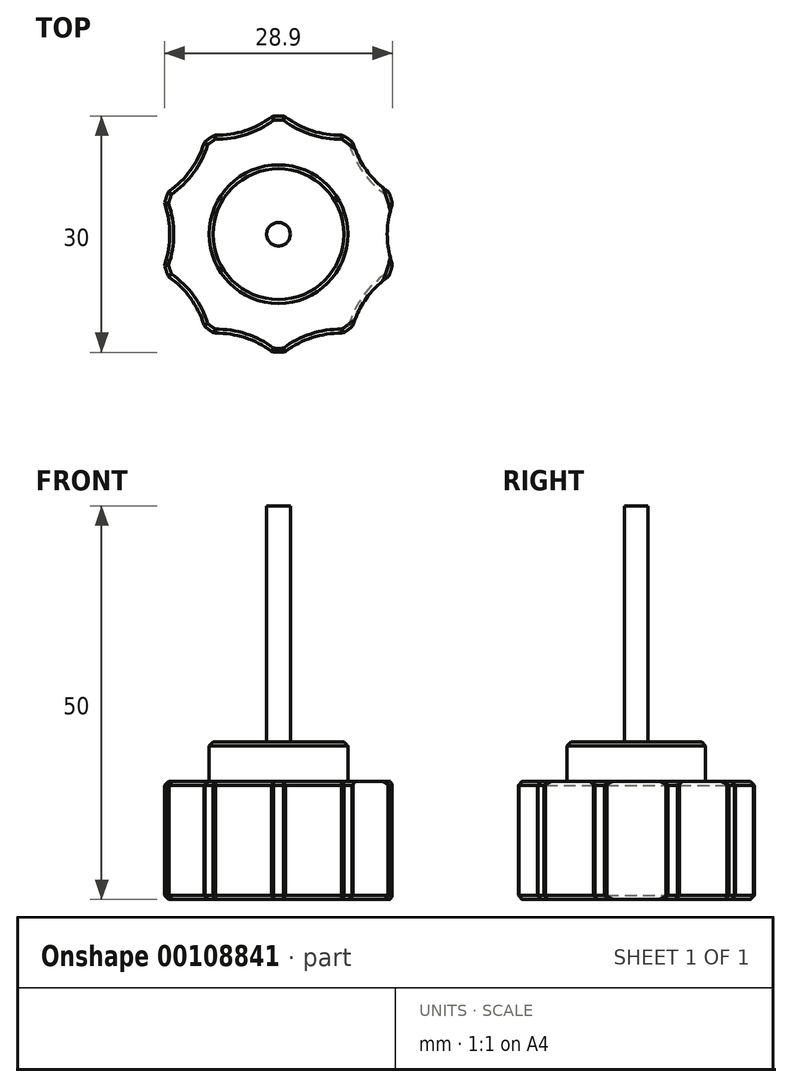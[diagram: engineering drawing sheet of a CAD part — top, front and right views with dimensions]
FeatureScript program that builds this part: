
annotation { "Feature Type Name" : "Feature", "Feature Type Description" : "" }
export const myFeature = defineFeature(function(context is Context, id is Id, definition is map)
    precondition{}
    {
        {
            var Q0;
            Q0=qCreatedBy(makeId("Top.planeOp"),FACE);
            var sketch = newSketch(context, id + "F0", { "sketchPlane" : qUnion([Q0])});
            skLineSegment(sketch, "E0", {"start": v(0, 24.73) * mm, "end": v(0, -28.06) * mm, "construction": true});
            skLineSegment(sketch, "E1", {"start": v(-17.48, 0) * mm, "end": v(21.6, 0) * mm, "construction": true});
            skArc(sketch, "E2", {"start": v(-14, 5.38) * mm, "mid": v(-14.27, 4.64) * mm, "end": v(-14.49, 3.88) * mm});
            skLineSegment(sketch, "E3", {"start": v(0, 0) * mm, "end": v(21.8, 5.84) * mm, "construction": true});
            skLineSegment(sketch, "E4.MirrorCS", {"start": v(0, 0) * mm, "end": v(21.8, -5.84) * mm, "construction": true});
            skArc(sketch, "E5", {"start": v(14.49, 3.88) * mm, "mid": v(13.81, 0) * mm, "end": v(14.49, -3.88) * mm});
            skLineSegment(sketch, "E6.anchor1", {"start": v(0, 0) * mm, "end": v(14.49, -3.88) * mm, "construction": true});
            skLineSegment(sketch, "E6.anchor2", {"start": v(0, 0) * mm, "end": v(14.49, -3.88) * mm, "construction": true});
            skArc(sketch, "E7.1.0", {"start": v(9.44, 11.66) * mm, "mid": v(11.17, 8.12) * mm, "end": v(14, 5.38) * mm});
            skArc(sketch, "E7.2.0", {"start": v(0.79, 14.98) * mm, "mid": v(4.27, 13.14) * mm, "end": v(8.17, 12.58) * mm});
            skArc(sketch, "E7.3.0", {"start": v(-8.17, 12.58) * mm, "mid": v(-4.27, 13.14) * mm, "end": v(-0.79, 14.98) * mm});
            skArc(sketch, "E7.4.0", {"start": v(-14, 5.38) * mm, "mid": v(-11.17, 8.12) * mm, "end": v(-9.44, 11.66) * mm});
            skArc(sketch, "E7.5.0", {"start": v(-14.49, -3.88) * mm, "mid": v(-13.81, 0) * mm, "end": v(-14.49, 3.88) * mm});
            skArc(sketch, "E7.6.0", {"start": v(-9.44, -11.66) * mm, "mid": v(-11.17, -8.12) * mm, "end": v(-14, -5.38) * mm});
            skArc(sketch, "E7.7.0", {"start": v(-0.79, -14.98) * mm, "mid": v(-4.27, -13.14) * mm, "end": v(-8.17, -12.58) * mm});
            skArc(sketch, "E7.8.0", {"start": v(8.17, -12.58) * mm, "mid": v(4.27, -13.14) * mm, "end": v(0.79, -14.98) * mm});
            skArc(sketch, "E7.9.0", {"start": v(14, -5.38) * mm, "mid": v(11.17, -8.12) * mm, "end": v(9.44, -11.66) * mm});
            skArc(sketch, "E8.trimOffspring", {"start": v(-8.17, 12.58) * mm, "mid": v(-8.82, 12.14) * mm, "end": v(-9.44, 11.66) * mm});
            skArc(sketch, "E9.trimOffspring", {"start": v(0.79, 14.98) * mm, "mid": v(0, 15) * mm, "end": v(-0.79, 14.98) * mm});
            skArc(sketch, "E10.trimOffspring", {"start": v(9.44, 11.66) * mm, "mid": v(8.82, 12.14) * mm, "end": v(8.17, 12.58) * mm});
            skArc(sketch, "E11.trimOffspring", {"start": v(14.49, 3.88) * mm, "mid": v(14.27, 4.64) * mm, "end": v(14, 5.38) * mm});
            skArc(sketch, "E12.trimOffspring", {"start": v(14, -5.38) * mm, "mid": v(14.27, -4.64) * mm, "end": v(14.49, -3.88) * mm});
            skArc(sketch, "E13.trimOffspring", {"start": v(8.17, -12.58) * mm, "mid": v(8.82, -12.14) * mm, "end": v(9.44, -11.66) * mm});
            skArc(sketch, "E14.trimOffspring", {"start": v(-0.79, -14.98) * mm, "mid": v(0, -15) * mm, "end": v(0.79, -14.98) * mm});
            skArc(sketch, "E15.trimOffspring", {"start": v(-9.44, -11.66) * mm, "mid": v(-8.82, -12.14) * mm, "end": v(-8.17, -12.58) * mm});
            skArc(sketch, "E16.trimOffspring", {"start": v(-14.49, -3.88) * mm, "mid": v(-14.27, -4.64) * mm, "end": v(-14, -5.38) * mm});
            skSolve(sketch);
        }
        {
            var Q0;
            Q0=makeQuery(id+"F0.imprint","IMPRINT",FACE,{"disambiguationData":[TD([[makeQuery(id+"F0.imprint","IMPRINT",EDGE,{"derivedFrom":sQuery(id+"F0.wireOp",EDGE,"E2")}),1.0]])]});
            extrude(context, id + "F1", {"entities" : qUnion([Q0]), "depth" : 15 * mm});
        }
        {
            var Q0;
            Q0=makeQuery(id+"F1.opExtrude","CAP_FACE",FACE,{"disambiguationData":[OSD([sQuery(id+"F0.wireOp",EDGE,"E2"),sQuery(id+"F0.wireOp",EDGE,"E5"),sQuery(id+"F0.wireOp",EDGE,"E7.1.0"),sQuery(id+"F0.wireOp",EDGE,"E7.2.0"),sQuery(id+"F0.wireOp",EDGE,"E7.3.0"),sQuery(id+"F0.wireOp",EDGE,"E7.4.0"),sQuery(id+"F0.wireOp",EDGE,"E7.5.0"),sQuery(id+"F0.wireOp",EDGE,"E7.6.0"),sQuery(id+"F0.wireOp",EDGE,"E7.7.0"),sQuery(id+"F0.wireOp",EDGE,"E7.8.0"),sQuery(id+"F0.wireOp",EDGE,"E7.9.0"),sQuery(id+"F0.wireOp",EDGE,"E8.trimOffspring"),sQuery(id+"F0.wireOp",EDGE,"E9.trimOffspring"),sQuery(id+"F0.wireOp",EDGE,"E10.trimOffspring"),sQuery(id+"F0.wireOp",EDGE,"E11.trimOffspring"),sQuery(id+"F0.wireOp",EDGE,"E12.trimOffspring"),sQuery(id+"F0.wireOp",EDGE,"E13.trimOffspring"),sQuery(id+"F0.wireOp",EDGE,"E14.trimOffspring"),sQuery(id+"F0.wireOp",EDGE,"E15.trimOffspring"),sQuery(id+"F0.wireOp",EDGE,"E16.trimOffspring")])],"isStart":false});
            cPlane(context, id + "F2", {"entities" : qUnion([Q0]), "cplaneType" : CPlaneType.OFFSET, "offset" : 0 * mm, "width" : 150 * mm, "height" : 150 * mm});
        }
        {
            var Q0;
            Q0=qCreatedBy(id+"F2.planeOp",FACE);
            var sketch = newSketch(context, id + "F3", { "sketchPlane" : qUnion([Q0])});
            skCircle(sketch, "E17", {"center": v(0, 0) * mm, "radius": 8.8 * mm});
            skSolve(sketch);
        }
        {
            var Q0;
            Q0 = qSketchRegion(id + "F3", true);
            extrude(context, id + "F4", {"entities" : qUnion([Q0]), "operationType" : NewBodyOperationType.ADD, "depth" : 5 * mm});
        }
        {
            var Q0;
            Q0=makeQuery(id+"F4.opExtrude","CAP_FACE",FACE,{"disambiguationData":[OSD([sQuery(id+"F3.wireOp",EDGE,"E17")])],"isStart":false});
            cPlane(context, id + "F5", {"entities" : qUnion([Q0]), "cplaneType" : CPlaneType.OFFSET, "offset" : 0 * mm, "width" : 150 * mm, "height" : 150 * mm});
        }
        {
            var Q0;
            Q0=qCreatedBy(id+"F5.planeOp",FACE);
            var sketch = newSketch(context, id + "F6", { "sketchPlane" : qUnion([Q0])});
            skCircle(sketch, "E18", {"center": v(0, 0) * mm, "radius": 1.5 * mm});
            skSolve(sketch);
        }
        {
            var Q0;
            Q0=makeQuery(id+"F6.imprint","IMPRINT",FACE,{"disambiguationData":[TD([[makeQuery(id+"F6.imprint","IMPRINT",EDGE,{"derivedFrom":sQuery(id+"F6.wireOp",EDGE,"E18")}),1.0]])]});
            extrude(context, id + "F7", {"entities" : qUnion([Q0]), "depth" : 30 * mm});
        }
        {
            var Q0;
            Q0=makeQuery(id+"F4.opExtrude","CAP_EDGE",EDGE,{"disambiguationData":[OSD([sQuery(id+"F3.wireOp",EDGE,"E17")])],"isStart":false});
            var Q1;
            Q1=makeQuery(id+"F1.opExtrude","CAP_EDGE",EDGE,{"disambiguationData":[OSD([sQuery(id+"F0.wireOp",EDGE,"E7.4.0")])],"isStart":false});
            var Q2;
            Q2=makeQuery(id+"F1.opExtrude","CAP_EDGE",EDGE,{"disambiguationData":[OSD([sQuery(id+"F0.wireOp",EDGE,"E7.5.0")])],"isStart":false});
            var Q3;
            Q3=makeQuery(id+"F1.opExtrude","CAP_EDGE",EDGE,{"disambiguationData":[OSD([sQuery(id+"F0.wireOp",EDGE,"E16.trimOffspring")])],"isStart":false});
            var Q4;
            Q4=makeQuery(id+"F1.opExtrude","CAP_EDGE",EDGE,{"disambiguationData":[OSD([sQuery(id+"F0.wireOp",EDGE,"E2")])],"isStart":false});
            var Q5;
            Q5=makeQuery(id+"F1.opExtrude","CAP_EDGE",EDGE,{"disambiguationData":[OSD([sQuery(id+"F0.wireOp",EDGE,"E13.trimOffspring")])],"isStart":true});
            var Q6;
            Q6=makeQuery(id+"F1.opExtrude","CAP_EDGE",EDGE,{"disambiguationData":[OSD([sQuery(id+"F0.wireOp",EDGE,"E7.6.0")])],"isStart":false});
            var Q7;
            Q7=makeQuery(id+"F1.opExtrude","CAP_EDGE",EDGE,{"disambiguationData":[OSD([sQuery(id+"F0.wireOp",EDGE,"E15.trimOffspring")])],"isStart":false});
            var Q8;
            Q8=makeQuery(id+"F1.opExtrude","CAP_EDGE",EDGE,{"disambiguationData":[OSD([sQuery(id+"F0.wireOp",EDGE,"E13.trimOffspring")])],"isStart":false});
            var Q9;
            Q9=makeQuery(id+"F1.opExtrude","CAP_EDGE",EDGE,{"disambiguationData":[OSD([sQuery(id+"F0.wireOp",EDGE,"E7.7.0")])],"isStart":false});
            var Q10;
            Q10=makeQuery(id+"F1.opExtrude","CAP_EDGE",EDGE,{"disambiguationData":[OSD([sQuery(id+"F0.wireOp",EDGE,"E14.trimOffspring")])],"isStart":false});
            var Q11;
            Q11=makeQuery(id+"F1.opExtrude","CAP_EDGE",EDGE,{"disambiguationData":[OSD([sQuery(id+"F0.wireOp",EDGE,"E7.8.0")])],"isStart":false});
            var Q12;
            Q12=makeQuery(id+"F1.opExtrude","SWEPT_EDGE",EDGE,{"disambiguationData":[OSD([sQuery(id+"F0.wireOp",EDGE,"E7.8.0"),sQuery(id+"F0.wireOp",EDGE,"E13.trimOffspring")])]});
            var Q13;
            Q13=makeQuery(id+"F1.opExtrude","SWEPT_EDGE",EDGE,{"disambiguationData":[OSD([sQuery(id+"F0.wireOp",EDGE,"E7.9.0"),sQuery(id+"F0.wireOp",EDGE,"E13.trimOffspring")])]});
            var Q14;
            Q14=makeQuery(id+"F1.opExtrude","CAP_EDGE",EDGE,{"disambiguationData":[OSD([sQuery(id+"F0.wireOp",EDGE,"E11.trimOffspring")])],"isStart":false});
            var Q15;
            Q15=makeQuery(id+"F1.opExtrude","CAP_EDGE",EDGE,{"disambiguationData":[OSD([sQuery(id+"F0.wireOp",EDGE,"E5")])],"isStart":true});
            var Q16;
            Q16=makeQuery(id+"F1.opExtrude","CAP_EDGE",EDGE,{"disambiguationData":[OSD([sQuery(id+"F0.wireOp",EDGE,"E12.trimOffspring")])],"isStart":true});
            var Q17;
            Q17=makeQuery(id+"F1.opExtrude","CAP_EDGE",EDGE,{"disambiguationData":[OSD([sQuery(id+"F0.wireOp",EDGE,"E12.trimOffspring")])],"isStart":false});
            var Q18;
            Q18=makeQuery(id+"F1.opExtrude","CAP_EDGE",EDGE,{"disambiguationData":[OSD([sQuery(id+"F0.wireOp",EDGE,"E5")])],"isStart":false});
            var Q19;
            Q19=makeQuery(id+"F1.opExtrude","CAP_EDGE",EDGE,{"disambiguationData":[OSD([sQuery(id+"F0.wireOp",EDGE,"E7.1.0")])],"isStart":true});
            var Q20;
            Q20=makeQuery(id+"F1.opExtrude","SWEPT_EDGE",EDGE,{"disambiguationData":[OSD([sQuery(id+"F0.wireOp",EDGE,"E7.9.0"),sQuery(id+"F0.wireOp",EDGE,"E12.trimOffspring")])]});
            var Q21;
            Q21=makeQuery(id+"F1.opExtrude","SWEPT_EDGE",EDGE,{"disambiguationData":[OSD([sQuery(id+"F0.wireOp",EDGE,"E5"),sQuery(id+"F0.wireOp",EDGE,"E12.trimOffspring")])]});
            var Q22;
            Q22=makeQuery(id+"F1.opExtrude","SWEPT_EDGE",EDGE,{"disambiguationData":[OSD([sQuery(id+"F0.wireOp",EDGE,"E5"),sQuery(id+"F0.wireOp",EDGE,"E11.trimOffspring")])]});
            var Q23;
            Q23=makeQuery(id+"F1.opExtrude","SWEPT_EDGE",EDGE,{"disambiguationData":[OSD([sQuery(id+"F0.wireOp",EDGE,"E7.1.0"),sQuery(id+"F0.wireOp",EDGE,"E11.trimOffspring")])]});
            var Q24;
            Q24=makeQuery(id+"F1.opExtrude","CAP_EDGE",EDGE,{"disambiguationData":[OSD([sQuery(id+"F0.wireOp",EDGE,"E11.trimOffspring")])],"isStart":true});
            var Q25;
            Q25=makeQuery(id+"F1.opExtrude","CAP_EDGE",EDGE,{"disambiguationData":[OSD([sQuery(id+"F0.wireOp",EDGE,"E7.9.0")])],"isStart":true});
            var Q26;
            Q26=makeQuery(id+"F1.opExtrude","CAP_EDGE",EDGE,{"disambiguationData":[OSD([sQuery(id+"F0.wireOp",EDGE,"E10.trimOffspring")])],"isStart":false});
            var Q27;
            Q27=makeQuery(id+"F1.opExtrude","CAP_EDGE",EDGE,{"disambiguationData":[OSD([sQuery(id+"F0.wireOp",EDGE,"E9.trimOffspring")])],"isStart":false});
            var Q28;
            Q28=makeQuery(id+"F1.opExtrude","CAP_EDGE",EDGE,{"disambiguationData":[OSD([sQuery(id+"F0.wireOp",EDGE,"E7.3.0")])],"isStart":false});
            var Q29;
            Q29=makeQuery(id+"F1.opExtrude","CAP_EDGE",EDGE,{"disambiguationData":[OSD([sQuery(id+"F0.wireOp",EDGE,"E7.3.0")])],"isStart":true});
            var Q30;
            Q30=makeQuery(id+"F1.opExtrude","CAP_EDGE",EDGE,{"disambiguationData":[OSD([sQuery(id+"F0.wireOp",EDGE,"E7.2.0")])],"isStart":true});
            var Q31;
            Q31=makeQuery(id+"F1.opExtrude","CAP_EDGE",EDGE,{"disambiguationData":[OSD([sQuery(id+"F0.wireOp",EDGE,"E8.trimOffspring")])],"isStart":true});
            var Q32;
            Q32=makeQuery(id+"F1.opExtrude","CAP_EDGE",EDGE,{"disambiguationData":[OSD([sQuery(id+"F0.wireOp",EDGE,"E7.2.0")])],"isStart":false});
            var Q33;
            Q33=makeQuery(id+"F1.opExtrude","CAP_EDGE",EDGE,{"disambiguationData":[OSD([sQuery(id+"F0.wireOp",EDGE,"E8.trimOffspring")])],"isStart":false});
            var Q34;
            Q34=makeQuery(id+"F1.opExtrude","CAP_EDGE",EDGE,{"disambiguationData":[OSD([sQuery(id+"F0.wireOp",EDGE,"E9.trimOffspring")])],"isStart":true});
            var Q35;
            Q35=makeQuery(id+"F1.opExtrude","CAP_EDGE",EDGE,{"disambiguationData":[OSD([sQuery(id+"F0.wireOp",EDGE,"E10.trimOffspring")])],"isStart":true});
            var Q36;
            Q36=makeQuery(id+"F1.opExtrude","SWEPT_EDGE",EDGE,{"disambiguationData":[OSD([sQuery(id+"F0.wireOp",EDGE,"E7.4.0"),sQuery(id+"F0.wireOp",EDGE,"E8.trimOffspring")])]});
            var Q37;
            Q37=makeQuery(id+"F1.opExtrude","SWEPT_EDGE",EDGE,{"disambiguationData":[OSD([sQuery(id+"F0.wireOp",EDGE,"E7.3.0"),sQuery(id+"F0.wireOp",EDGE,"E9.trimOffspring")])]});
            var Q38;
            Q38=makeQuery(id+"F1.opExtrude","SWEPT_EDGE",EDGE,{"disambiguationData":[OSD([sQuery(id+"F0.wireOp",EDGE,"E7.2.0"),sQuery(id+"F0.wireOp",EDGE,"E10.trimOffspring")])]});
            var Q39;
            Q39=makeQuery(id+"F1.opExtrude","SWEPT_EDGE",EDGE,{"disambiguationData":[OSD([sQuery(id+"F0.wireOp",EDGE,"E7.2.0"),sQuery(id+"F0.wireOp",EDGE,"E9.trimOffspring")])]});
            var Q40;
            Q40=makeQuery(id+"F1.opExtrude","SWEPT_EDGE",EDGE,{"disambiguationData":[OSD([sQuery(id+"F0.wireOp",EDGE,"E7.1.0"),sQuery(id+"F0.wireOp",EDGE,"E10.trimOffspring")])]});
            var Q41;
            Q41=makeQuery(id+"F1.opExtrude","SWEPT_EDGE",EDGE,{"disambiguationData":[OSD([sQuery(id+"F0.wireOp",EDGE,"E7.3.0"),sQuery(id+"F0.wireOp",EDGE,"E8.trimOffspring")])]});
            var Q42;
            Q42=makeQuery(id+"F1.opExtrude","SWEPT_EDGE",EDGE,{"disambiguationData":[OSD([sQuery(id+"F0.wireOp",EDGE,"E7.7.0"),sQuery(id+"F0.wireOp",EDGE,"E14.trimOffspring")])]});
            var Q43;
            Q43=makeQuery(id+"F1.opExtrude","SWEPT_EDGE",EDGE,{"disambiguationData":[OSD([sQuery(id+"F0.wireOp",EDGE,"E7.8.0"),sQuery(id+"F0.wireOp",EDGE,"E14.trimOffspring")])]});
            var Q44;
            Q44=makeQuery(id+"F1.opExtrude","SWEPT_EDGE",EDGE,{"disambiguationData":[OSD([sQuery(id+"F0.wireOp",EDGE,"E7.7.0"),sQuery(id+"F0.wireOp",EDGE,"E15.trimOffspring")])]});
            var Q45;
            Q45=makeQuery(id+"F1.opExtrude","SWEPT_EDGE",EDGE,{"disambiguationData":[OSD([sQuery(id+"F0.wireOp",EDGE,"E7.6.0"),sQuery(id+"F0.wireOp",EDGE,"E15.trimOffspring")])]});
            var Q46;
            Q46=makeQuery(id+"F1.opExtrude","SWEPT_EDGE",EDGE,{"disambiguationData":[OSD([sQuery(id+"F0.wireOp",EDGE,"E7.6.0"),sQuery(id+"F0.wireOp",EDGE,"E16.trimOffspring")])]});
            var Q47;
            Q47=makeQuery(id+"F1.opExtrude","SWEPT_EDGE",EDGE,{"disambiguationData":[OSD([sQuery(id+"F0.wireOp",EDGE,"E7.5.0"),sQuery(id+"F0.wireOp",EDGE,"E16.trimOffspring")])]});
            var Q48;
            Q48=makeQuery(id+"F1.opExtrude","SWEPT_EDGE",EDGE,{"disambiguationData":[OSD([sQuery(id+"F0.wireOp",EDGE,"E2"),sQuery(id+"F0.wireOp",EDGE,"E7.5.0")])]});
            var Q49;
            Q49=makeQuery(id+"F1.opExtrude","SWEPT_EDGE",EDGE,{"disambiguationData":[OSD([sQuery(id+"F0.wireOp",EDGE,"E2"),sQuery(id+"F0.wireOp",EDGE,"E7.4.0")])]});
            var Q50;
            Q50=makeQuery(id+"F1.opExtrude","CAP_EDGE",EDGE,{"disambiguationData":[OSD([sQuery(id+"F0.wireOp",EDGE,"E7.5.0")])],"isStart":true});
            var Q51;
            Q51=makeQuery(id+"F1.opExtrude","CAP_EDGE",EDGE,{"disambiguationData":[OSD([sQuery(id+"F0.wireOp",EDGE,"E2")])],"isStart":true});
            var Q52;
            Q52=makeQuery(id+"F1.opExtrude","CAP_EDGE",EDGE,{"disambiguationData":[OSD([sQuery(id+"F0.wireOp",EDGE,"E7.4.0")])],"isStart":true});
            var Q53;
            Q53=makeQuery(id+"F1.opExtrude","CAP_EDGE",EDGE,{"disambiguationData":[OSD([sQuery(id+"F0.wireOp",EDGE,"E7.6.0")])],"isStart":true});
            var Q54;
            Q54=makeQuery(id+"F1.opExtrude","CAP_EDGE",EDGE,{"disambiguationData":[OSD([sQuery(id+"F0.wireOp",EDGE,"E7.7.0")])],"isStart":true});
            var Q55;
            Q55=makeQuery(id+"F1.opExtrude","CAP_EDGE",EDGE,{"disambiguationData":[OSD([sQuery(id+"F0.wireOp",EDGE,"E7.8.0")])],"isStart":true});
            var Q56;
            Q56=makeQuery(id+"F1.opExtrude","SWEPT_FACE",FACE,{"disambiguationData":[OSD([sQuery(id+"F0.wireOp",EDGE,"E14.trimOffspring")])]});
            var Q57;
            Q57=makeQuery(id+"F1.opExtrude","SWEPT_FACE",FACE,{"disambiguationData":[OSD([sQuery(id+"F0.wireOp",EDGE,"E15.trimOffspring")])]});
            var Q58;
            Q58=makeQuery(id+"F1.opExtrude","SWEPT_FACE",FACE,{"disambiguationData":[OSD([sQuery(id+"F0.wireOp",EDGE,"E16.trimOffspring")])]});
            chamfer(context, id + "F8", {"entities" : qUnion([Q0, Q1, Q2, Q3, Q4, Q5, Q6, Q7, Q8, Q9, Q10, Q11, Q12, Q13, Q14, Q15, Q16, Q17, Q18, Q19, Q20, Q21, Q22, Q23, Q24, Q25, Q26, Q27, Q28, Q29, Q30, Q31, Q32, Q33, Q34, Q35, Q36, Q37, Q38, Q39, Q40, Q41, Q42, Q43, Q44, Q45, Q46, Q47, Q48, Q49, Q50, Q51, Q52, Q53, Q54, Q55, Q56, Q57, Q58]), "width" : 0.5 * mm, "tangentPropagation" : true});
        }
    });
